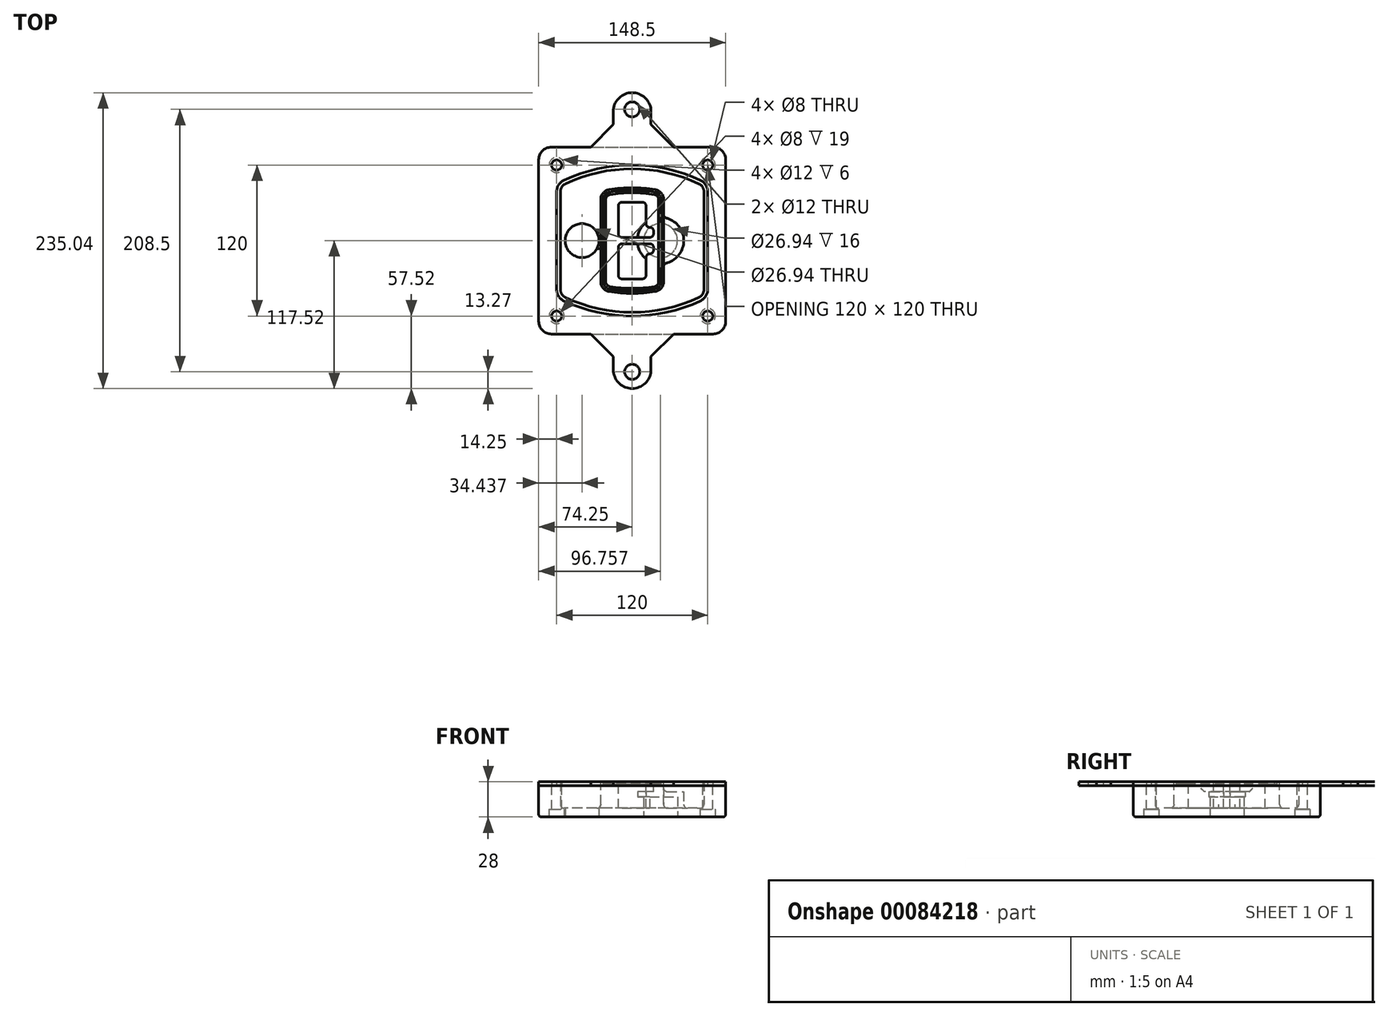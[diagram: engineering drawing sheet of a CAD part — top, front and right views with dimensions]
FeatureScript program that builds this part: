
annotation { "Feature Type Name" : "Feature", "Feature Type Description" : "" }
export const myFeature = defineFeature(function(context is Context, id is Id, definition is map)
    precondition{}
    {
        {
            var Q0;
            Q0=qCreatedBy(makeId("Top.planeOp"),FACE);
            var sketch = newSketch(context, id + "F0", { "sketchPlane" : qUnion([Q0])});
            skPoint(sketch, "E0.rect.middle", {"position": v(0, 0) * mm});
            skLineSegment(sketch, "E1.bottom", {"start": v(-64.25, -74.25) * mm, "end": v(64.25, -74.25) * mm});
            skLineSegment(sketch, "E1.top", {"start": v(-64.25, 74.25) * mm, "end": v(64.25, 74.25) * mm});
            skLineSegment(sketch, "E1.left", {"start": v(-74.25, -64.25) * mm, "end": v(-74.25, 64.25) * mm});
            skLineSegment(sketch, "E1.right", {"start": v(74.25, -64.25) * mm, "end": v(74.25, 64.25) * mm});
            skLineSegment(sketch, "E2", {"start": v(-74.25, 74.25) * mm, "end": v(74.25, -74.25) * mm, "construction": true});
            skLineSegment(sketch, "E3", {"start": v(74.25, 74.25) * mm, "end": v(-74.25, -74.25) * mm, "construction": true});
            skCircle(sketch, "E4", {"center": v(-60, 60) * mm, "radius": 4 * mm});
            skCircle(sketch, "E5", {"center": v(60, 60) * mm, "radius": 4 * mm});
            skCircle(sketch, "E6", {"center": v(60, -60) * mm, "radius": 4 * mm});
            skCircle(sketch, "E7", {"center": v(-60, -60) * mm, "radius": 4 * mm});
            skLineSegment(sketch, "E8", {"start": v(-60, 60) * mm, "end": v(60, 60) * mm, "construction": true});
            skLineSegment(sketch, "E9", {"start": v(60, 60) * mm, "end": v(60, -60) * mm, "construction": true});
            skLineSegment(sketch, "E10", {"start": v(60, -60) * mm, "end": v(-60, -60) * mm, "construction": true});
            skLineSegment(sketch, "E11", {"start": v(-60, -60) * mm, "end": v(-60, 60) * mm, "construction": true});
            skLineSegment(sketch, "E12", {"start": v(-60, 38.83) * mm, "end": v(-60, -38.83) * mm});
            skLineSegment(sketch, "E13", {"start": v(60, 38.83) * mm, "end": v(60, -38.83) * mm});
            skArc(sketch, "E14", {"start": v(54.26, 47.88) * mm, "mid": v(0, 60) * mm, "end": v(-54.26, 47.88) * mm});
            skArc(sketch, "E15", {"start": v(-54.26, -47.88) * mm, "mid": v(0, -60) * mm, "end": v(54.26, -47.88) * mm});
            skLineSegment(sketch, "E16", {"start": v(-60, 0) * mm, "end": v(60, 0) * mm, "construction": true});
            skPoint(sketch, "E17.visualSharp", {"position": v(-60, -45) * mm});
            skArc(sketch, "E17.filletArc", {"start": v(-60, -38.83) * mm, "mid": v(-58.44, -44.2) * mm, "end": v(-54.26, -47.88) * mm});
            skPoint(sketch, "E18.visualSharp", {"position": v(-60, 45) * mm});
            skArc(sketch, "E18.filletArc", {"start": v(-54.26, 47.88) * mm, "mid": v(-58.44, 44.2) * mm, "end": v(-60, 38.83) * mm});
            skPoint(sketch, "E19.visualSharp", {"position": v(60, 45) * mm});
            skArc(sketch, "E19.filletArc", {"start": v(60, 38.83) * mm, "mid": v(58.44, 44.2) * mm, "end": v(54.26, 47.88) * mm});
            skPoint(sketch, "E20.visualSharp", {"position": v(60, -45) * mm});
            skArc(sketch, "E20.filletArc", {"start": v(54.26, -47.88) * mm, "mid": v(58.44, -44.2) * mm, "end": v(60, -38.83) * mm});
            skPoint(sketch, "E21.visualSharp", {"position": v(-74.25, 74.25) * mm});
            skArc(sketch, "E21.filletArc", {"start": v(-64.25, 74.25) * mm, "mid": v(-71.32, 71.32) * mm, "end": v(-74.25, 64.25) * mm});
            skPoint(sketch, "E22.visualSharp", {"position": v(74.25, 74.25) * mm});
            skArc(sketch, "E22.filletArc", {"start": v(74.25, 64.25) * mm, "mid": v(71.32, 71.32) * mm, "end": v(64.25, 74.25) * mm});
            skPoint(sketch, "E23.visualSharp", {"position": v(74.25, -74.25) * mm});
            skArc(sketch, "E23.filletArc", {"start": v(64.25, -74.25) * mm, "mid": v(71.32, -71.32) * mm, "end": v(74.25, -64.25) * mm});
            skPoint(sketch, "E24.visualSharp", {"position": v(-74.25, -74.25) * mm});
            skArc(sketch, "E24.filletArc", {"start": v(-74.25, -64.25) * mm, "mid": v(-71.32, -71.32) * mm, "end": v(-64.25, -74.25) * mm});
            skArc(sketch, "E25.0", {"start": v(57, 38.83) * mm, "mid": v(55.9, 42.58) * mm, "end": v(52.98, 45.17) * mm});
            skLineSegment(sketch, "E25.1", {"start": v(57, 38.83) * mm, "end": v(57, -38.83) * mm});
            skArc(sketch, "E25.2", {"start": v(52.98, -45.17) * mm, "mid": v(55.9, -42.58) * mm, "end": v(57, -38.83) * mm});
            skArc(sketch, "E25.3", {"start": v(-52.98, -45.17) * mm, "mid": v(0, -57) * mm, "end": v(52.98, -45.17) * mm});
            skArc(sketch, "E25.4", {"start": v(-57, -38.83) * mm, "mid": v(-55.9, -42.58) * mm, "end": v(-52.98, -45.17) * mm});
            skArc(sketch, "E25.5", {"start": v(52.98, 45.17) * mm, "mid": v(0, 57) * mm, "end": v(-52.98, 45.17) * mm});
            skLineSegment(sketch, "E25.6", {"start": v(-57, 38.83) * mm, "end": v(-57, -38.83) * mm});
            skArc(sketch, "E25.7", {"start": v(-52.98, 45.17) * mm, "mid": v(-55.9, 42.58) * mm, "end": v(-57, 38.83) * mm});
            skArc(sketch, "E26.0", {"start": v(-55.96, 51.5) * mm, "mid": v(-61.82, 46.33) * mm, "end": v(-64, 38.83) * mm});
            skArc(sketch, "E26.1", {"start": v(55.96, 51.5) * mm, "mid": v(0, 64) * mm, "end": v(-55.96, 51.5) * mm});
            skArc(sketch, "E26.2", {"start": v(64, 38.83) * mm, "mid": v(61.82, 46.33) * mm, "end": v(55.96, 51.5) * mm});
            skLineSegment(sketch, "E26.3", {"start": v(64, 38.83) * mm, "end": v(64, -38.83) * mm});
            skArc(sketch, "E26.4", {"start": v(55.96, -51.5) * mm, "mid": v(61.82, -46.33) * mm, "end": v(64, -38.83) * mm});
            skLineSegment(sketch, "E26.5", {"start": v(-64, 38.83) * mm, "end": v(-64, -38.83) * mm});
            skArc(sketch, "E26.6", {"start": v(-55.96, -51.5) * mm, "mid": v(0, -64) * mm, "end": v(55.96, -51.5) * mm});
            skArc(sketch, "E26.7", {"start": v(-64, -38.83) * mm, "mid": v(-61.82, -46.33) * mm, "end": v(-55.96, -51.5) * mm});
            skSolve(sketch);
        }
        {
            var Q0;
            Q0=makeQuery(id+"F0.imprint","IMPRINT",FACE,{"disambiguationData":[TD([[makeQuery(id+"F0.imprint","IMPRINT",EDGE,{"derivedFrom":sQuery(id+"F0.wireOp",EDGE,"E1.bottom")}),1.0]])]});
            var Q1;
            Q1=makeQuery(id+"F0.imprint","IMPRINT",FACE,{"disambiguationData":[TD([[makeQuery(id+"F0.imprint","IMPRINT",EDGE,{"derivedFrom":sQuery(id+"F0.wireOp",EDGE,"E12")}),1.0]])]});
            var Q2;
            Q2=makeQuery(id+"F0.imprint","IMPRINT",FACE,{"disambiguationData":[TD([[makeQuery(id+"F0.imprint","IMPRINT",EDGE,{"derivedFrom":sQuery(id+"F0.wireOp",EDGE,"E25.0")}),1.0]])]});
            var Q3;
            Q3=makeQuery(id+"F0.imprint","IMPRINT",FACE,{"disambiguationData":[TD([[makeQuery(id+"F0.imprint","IMPRINT",EDGE,{"derivedFrom":sQuery(id+"F0.wireOp",EDGE,"E12")}),-1.0]])]});
            extrude(context, id + "F1", {"entities" : qUnion([Q0, Q1, Q2, Q3]), "oppositeDirection" : true, "depth" : 25 * mm});
        }
        {
            var Q0;
            Q0=makeQuery(id+"F0.imprint","IMPRINT",FACE,{"disambiguationData":[TD([[makeQuery(id+"F0.imprint","IMPRINT",EDGE,{"derivedFrom":sQuery(id+"F0.wireOp",EDGE,"E12")}),1.0]])]});
            extrude(context, id + "F2", {"entities" : qUnion([Q0]), "operationType" : NewBodyOperationType.ADD, "depth" : 3 * mm});
        }
        {
            var Q0;
            Q0=makeQuery(id+"F0.imprint","IMPRINT",FACE,{"disambiguationData":[TD([[makeQuery(id+"F0.imprint","IMPRINT",EDGE,{"derivedFrom":sQuery(id+"F0.wireOp",EDGE,"E25.0")}),1.0]])]});
            extrude(context, id + "F3", {"entities" : qUnion([Q0]), "operationType" : NewBodyOperationType.REMOVE, "oppositeDirection" : true, "depth" : 18 * mm});
        }
        {
            var Q0;
            Q0=makeQuery(id+"F2.opExtrude","CAP_FACE",FACE,{"disambiguationData":[OSD([sQuery(id+"F0.wireOp",EDGE,"E12"),sQuery(id+"F0.wireOp",EDGE,"E13"),sQuery(id+"F0.wireOp",EDGE,"E14"),sQuery(id+"F0.wireOp",EDGE,"E15"),sQuery(id+"F0.wireOp",EDGE,"E17.filletArc"),sQuery(id+"F0.wireOp",EDGE,"E18.filletArc"),sQuery(id+"F0.wireOp",EDGE,"E19.filletArc"),sQuery(id+"F0.wireOp",EDGE,"E20.filletArc"),sQuery(id+"F0.wireOp",EDGE,"E25.0"),sQuery(id+"F0.wireOp",EDGE,"E25.1"),sQuery(id+"F0.wireOp",EDGE,"E25.2"),sQuery(id+"F0.wireOp",EDGE,"E25.3"),sQuery(id+"F0.wireOp",EDGE,"E25.4"),sQuery(id+"F0.wireOp",EDGE,"E25.5"),sQuery(id+"F0.wireOp",EDGE,"E25.6"),sQuery(id+"F0.wireOp",EDGE,"E25.7")])],"isStart":false});
            var sketch = newSketch(context, id + "F4", { "sketchPlane" : qUnion([Q0])});
            skArc(sketch, "E27.0", {"start": v(-18.34, -40.45) * mm, "mid": v(0, -42) * mm, "end": v(18.34, -40.45) * mm});
            skArc(sketch, "E28.0", {"start": v(18.34, 40.45) * mm, "mid": v(0, 42) * mm, "end": v(-18.34, 40.45) * mm});
            skLineSegment(sketch, "E29", {"start": v(-25, 32.57) * mm, "end": v(-25, -32.57) * mm});
            skLineSegment(sketch, "E30", {"start": v(25, 32.57) * mm, "end": v(25, -32.57) * mm});
            skLineSegment(sketch, "E31", {"start": v(-25, 39.1) * mm, "end": v(25, 39.1) * mm, "construction": true});
            skLineSegment(sketch, "E32", {"start": v(-25, -39.1) * mm, "end": v(25, -39.1) * mm, "construction": true});
            skPoint(sketch, "E33.visualSharp", {"position": v(-25, 39.1) * mm});
            skArc(sketch, "E33.filletArc", {"start": v(-18.34, 40.45) * mm, "mid": v(-23.11, 37.73) * mm, "end": v(-25, 32.57) * mm});
            skPoint(sketch, "E34.visualSharp", {"position": v(25, 39.1) * mm});
            skArc(sketch, "E34.filletArc", {"start": v(25, 32.57) * mm, "mid": v(23.11, 37.73) * mm, "end": v(18.34, 40.45) * mm});
            skPoint(sketch, "E35.visualSharp", {"position": v(25, -39.1) * mm});
            skArc(sketch, "E35.filletArc", {"start": v(18.34, -40.45) * mm, "mid": v(23.11, -37.73) * mm, "end": v(25, -32.57) * mm});
            skPoint(sketch, "E36.visualSharp", {"position": v(-25, -39.1) * mm});
            skArc(sketch, "E36.filletArc", {"start": v(-25, -32.57) * mm, "mid": v(-23.11, -37.73) * mm, "end": v(-18.34, -40.45) * mm});
            skArc(sketch, "E37.0", {"start": v(52.98, 45.17) * mm, "mid": v(0, 57) * mm, "end": v(-52.98, 45.17) * mm});
            skArc(sketch, "E37.1", {"start": v(-52.98, 45.17) * mm, "mid": v(-55.9, 42.58) * mm, "end": v(-57, 38.83) * mm});
            skLineSegment(sketch, "E37.2", {"start": v(-57, 38.83) * mm, "end": v(-57, -38.83) * mm});
            skArc(sketch, "E37.3", {"start": v(-57, -38.83) * mm, "mid": v(-55.9, -42.58) * mm, "end": v(-52.98, -45.17) * mm});
            skArc(sketch, "E37.4", {"start": v(-52.98, -45.17) * mm, "mid": v(0, -57) * mm, "end": v(52.98, -45.17) * mm});
            skArc(sketch, "E37.5", {"start": v(52.98, -45.17) * mm, "mid": v(55.9, -42.58) * mm, "end": v(57, -38.83) * mm});
            skLineSegment(sketch, "E37.6", {"start": v(57, 38.83) * mm, "end": v(57, -38.83) * mm});
            skArc(sketch, "E37.7", {"start": v(57, 38.83) * mm, "mid": v(55.9, 42.58) * mm, "end": v(52.98, 45.17) * mm});
            skLineSegment(sketch, "E38.0", {"start": v(23, 32.57) * mm, "end": v(23, -32.57) * mm});
            skArc(sketch, "E38.1", {"start": v(18, -38.48) * mm, "mid": v(21.58, -36.44) * mm, "end": v(23, -32.57) * mm});
            skArc(sketch, "E38.2", {"start": v(-18, -38.48) * mm, "mid": v(0, -40) * mm, "end": v(18, -38.48) * mm});
            skArc(sketch, "E38.3", {"start": v(-23, -32.57) * mm, "mid": v(-21.58, -36.44) * mm, "end": v(-18, -38.48) * mm});
            skLineSegment(sketch, "E38.4", {"start": v(-23, 32.57) * mm, "end": v(-23, -32.57) * mm});
            skArc(sketch, "E38.5", {"start": v(23, 32.57) * mm, "mid": v(21.58, 36.44) * mm, "end": v(18, 38.48) * mm});
            skArc(sketch, "E38.6", {"start": v(-18, 38.48) * mm, "mid": v(-21.58, 36.44) * mm, "end": v(-23, 32.57) * mm});
            skArc(sketch, "E38.7", {"start": v(18, 38.48) * mm, "mid": v(0, 40) * mm, "end": v(-18, 38.48) * mm});
            skArc(sketch, "E39.0", {"start": v(21, 32.57) * mm, "mid": v(20.06, 35.15) * mm, "end": v(17.67, 36.5) * mm});
            skLineSegment(sketch, "E39.1", {"start": v(21, 32.57) * mm, "end": v(21, -32.57) * mm});
            skArc(sketch, "E39.2", {"start": v(17.67, -36.5) * mm, "mid": v(20.06, -35.15) * mm, "end": v(21, -32.57) * mm});
            skArc(sketch, "E39.3", {"start": v(-17.67, -36.5) * mm, "mid": v(0, -38) * mm, "end": v(17.67, -36.5) * mm});
            skArc(sketch, "E39.4", {"start": v(-21, -32.57) * mm, "mid": v(-20.06, -35.15) * mm, "end": v(-17.67, -36.5) * mm});
            skArc(sketch, "E39.5", {"start": v(17.67, 36.5) * mm, "mid": v(0, 38) * mm, "end": v(-17.67, 36.5) * mm});
            skLineSegment(sketch, "E39.6", {"start": v(-21, 32.57) * mm, "end": v(-21, -32.57) * mm});
            skArc(sketch, "E39.7", {"start": v(-17.67, 36.5) * mm, "mid": v(-20.06, 35.15) * mm, "end": v(-21, 32.57) * mm});
            skLineSegment(sketch, "E40", {"start": v(-25, 0) * mm, "end": v(25, 0) * mm, "construction": true});
            skLineSegment(sketch, "E41", {"start": v(-11, 5.5) * mm, "end": v(-11, 27.5) * mm});
            skLineSegment(sketch, "E42", {"start": v(-8, 30.5) * mm, "end": v(8, 30.5) * mm});
            skLineSegment(sketch, "E43", {"start": v(11, 27.5) * mm, "end": v(11, 13.5) * mm});
            skLineSegment(sketch, "E44", {"start": v(14, 10.5) * mm, "end": v(14, 10.5) * mm});
            skLineSegment(sketch, "E45", {"start": v(17, 7.5) * mm, "end": v(17, 5.5) * mm});
            skLineSegment(sketch, "E46", {"start": v(14, 2.5) * mm, "end": v(-8, 2.5) * mm});
            skPoint(sketch, "E47.visualSharp", {"position": v(-11, 30.5) * mm});
            skArc(sketch, "E47.filletArc", {"start": v(-8, 30.5) * mm, "mid": v(-10.12, 29.62) * mm, "end": v(-11, 27.5) * mm});
            skPoint(sketch, "E48.visualSharp", {"position": v(11, 30.5) * mm});
            skArc(sketch, "E48.filletArc", {"start": v(11, 27.5) * mm, "mid": v(10.12, 29.62) * mm, "end": v(8, 30.5) * mm});
            skPoint(sketch, "E49.visualSharp", {"position": v(11, 10.5) * mm});
            skArc(sketch, "E49.filletArc", {"start": v(11, 13.5) * mm, "mid": v(11.88, 11.38) * mm, "end": v(14, 10.5) * mm});
            skPoint(sketch, "E50.visualSharp", {"position": v(17, 10.5) * mm});
            skArc(sketch, "E50.filletArc", {"start": v(17, 7.5) * mm, "mid": v(16.12, 9.62) * mm, "end": v(14, 10.5) * mm});
            skPoint(sketch, "E51.visualSharp", {"position": v(17, 2.5) * mm});
            skArc(sketch, "E51.filletArc", {"start": v(14, 2.5) * mm, "mid": v(16.12, 3.38) * mm, "end": v(17, 5.5) * mm});
            skPoint(sketch, "E52.visualSharp", {"position": v(-11, 2.5) * mm});
            skArc(sketch, "E52.filletArc", {"start": v(-11, 5.5) * mm, "mid": v(-10.12, 3.38) * mm, "end": v(-8, 2.5) * mm});
            skLineSegment(sketch, "E53.0.MirrorCS", {"start": v(14, -2.5) * mm, "end": v(-8, -2.5) * mm});
            skArc(sketch, "E54.0.MirrorCS", {"start": v(-11, -5.5) * mm, "mid": v(-10.12, -3.38) * mm, "end": v(-8, -2.5) * mm});
            skLineSegment(sketch, "E55.0.MirrorCS", {"start": v(-11, -5.5) * mm, "end": v(-11, -27.5) * mm});
            skArc(sketch, "E56.0.MirrorCS", {"start": v(-8, -30.5) * mm, "mid": v(-10.12, -29.62) * mm, "end": v(-11, -27.5) * mm});
            skLineSegment(sketch, "E57.0.MirrorCS", {"start": v(-8, -30.5) * mm, "end": v(8, -30.5) * mm});
            skArc(sketch, "E58.0.MirrorCS", {"start": v(11, -27.5) * mm, "mid": v(10.12, -29.62) * mm, "end": v(8, -30.5) * mm});
            skLineSegment(sketch, "E59.0.MirrorCS", {"start": v(11, -27.5) * mm, "end": v(11, -13.5) * mm});
            skArc(sketch, "E60.0.MirrorCS", {"start": v(11, -13.5) * mm, "mid": v(11.88, -11.38) * mm, "end": v(14, -10.5) * mm});
            skArc(sketch, "E61.0.MirrorCS", {"start": v(17, -7.5) * mm, "mid": v(16.12, -9.62) * mm, "end": v(14, -10.5) * mm});
            skLineSegment(sketch, "E62.0.MirrorCS", {"start": v(17, -7.5) * mm, "end": v(17, -5.5) * mm});
            skArc(sketch, "E63.0.MirrorCS", {"start": v(14, -2.5) * mm, "mid": v(16.12, -3.38) * mm, "end": v(17, -5.5) * mm});
            skSolve(sketch);
        }
        {
            var Q0;
            Q0=makeQuery(id+"F4.imprint","IMPRINT",FACE,{"disambiguationData":[TD([[makeQuery(id+"F4.imprint","IMPRINT",EDGE,{"derivedFrom":sQuery(id+"F4.wireOp",EDGE,"E27.0")}),1.0]])]});
            var Q1;
            Q1=makeQuery(id+"F4.imprint","IMPRINT",FACE,{"disambiguationData":[TD([[makeQuery(id+"F4.imprint","IMPRINT",EDGE,{"derivedFrom":sQuery(id+"F4.wireOp",EDGE,"E38.0")}),-1.0]])]});
            var Q2;
            Q2=makeQuery(id+"F4.imprint","IMPRINT",FACE,{"disambiguationData":[TD([[makeQuery(id+"F4.imprint","IMPRINT",EDGE,{"derivedFrom":sQuery(id+"F4.wireOp",EDGE,"E39.0")}),1.0]])]});
            extrude(context, id + "F5", {"entities" : qUnion([Q0, Q1, Q2]), "operationType" : NewBodyOperationType.ADD, "endBound" : BoundingType.UP_TO_NEXT, "oppositeDirection" : true, "depth" : 25 * mm});
        }
        {
            var Q0;
            Q0=makeQuery(id+"F4.imprint","IMPRINT",FACE,{"disambiguationData":[TD([[makeQuery(id+"F4.imprint","IMPRINT",EDGE,{"derivedFrom":sQuery(id+"F4.wireOp",EDGE,"E38.0")}),-1.0]])]});
            extrude(context, id + "F6", {"entities" : qUnion([Q0]), "operationType" : NewBodyOperationType.REMOVE, "oppositeDirection" : true, "depth" : 2 * mm});
        }
        {
            var Q0;
            Q0=makeQuery(id+"F1.opExtrude","CAP_FACE",FACE,{"disambiguationData":[OSD([sQuery(id+"F0.wireOp",EDGE,"E1.bottom"),sQuery(id+"F0.wireOp",EDGE,"E1.top"),sQuery(id+"F0.wireOp",EDGE,"E1.left"),sQuery(id+"F0.wireOp",EDGE,"E1.right"),sQuery(id+"F0.wireOp",EDGE,"E4"),sQuery(id+"F0.wireOp",EDGE,"E5"),sQuery(id+"F0.wireOp",EDGE,"E6"),sQuery(id+"F0.wireOp",EDGE,"E7"),sQuery(id+"F0.wireOp",EDGE,"E21.filletArc"),sQuery(id+"F0.wireOp",EDGE,"E22.filletArc"),sQuery(id+"F0.wireOp",EDGE,"E23.filletArc"),sQuery(id+"F0.wireOp",EDGE,"E24.filletArc")])],"isStart":false});
            var sketch = newSketch(context, id + "F7", { "sketchPlane" : qUnion([Q0])});
            skCircle(sketch, "E64", {"center": v(22.5, 0) * mm, "radius": 13.47 * mm});
            skCircle(sketch, "E65", {"center": v(-39.81, 0) * mm, "radius": 13.47 * mm});
            skLineSegment(sketch, "E66", {"start": v(74.25, 0) * mm, "end": v(-74.25, 0) * mm});
            skCircle(sketch, "E67", {"center": v(22.5, 0) * mm, "radius": 18.47 * mm});
            skCircle(sketch, "E68", {"center": v(60, -60) * mm, "radius": 6 * mm});
            skCircle(sketch, "E69", {"center": v(-60, -60) * mm, "radius": 6 * mm});
            skCircle(sketch, "E70", {"center": v(-60, 60) * mm, "radius": 6 * mm});
            skCircle(sketch, "E71", {"center": v(60, 60) * mm, "radius": 6 * mm});
            skSolve(sketch);
        }
        {
            var Q0;
            {var subQ1=sQuery(id+"F7.wireOp",EDGE,"E66");var subQ4=sQuery(id+"F7.wireOp",EDGE,"E64");var subQ6=makeQuery(id+"F7.imprint","INTERSECT",VERTEX,{"disambiguationData":[OD(0.0)],"derivedFrom":[subQ4,subQ1]});Q0=makeQuery(id+"F7.imprint","IMPRINT",FACE,{"disambiguationData":[TD([[makeQuery(id+"F7.imprint","IMPRINT",EDGE,{"disambiguationData":[TD([[subQ6,-1.0]])],"derivedFrom":subQ4}),-1.0]])]});}
            var Q1;
            {var subQ0=sQuery(id+"F7.wireOp",EDGE,"E66");var subQ1=sQuery(id+"F7.wireOp",EDGE,"E64");var subQ3=makeQuery(id+"F7.imprint","INTERSECT",VERTEX,{"disambiguationData":[OD(0.0)],"derivedFrom":[subQ1,subQ0]});Q1=makeQuery(id+"F7.imprint","IMPRINT",FACE,{"disambiguationData":[TD([[makeQuery(id+"F7.imprint","IMPRINT",EDGE,{"disambiguationData":[TD([[subQ3,-1.0]])],"derivedFrom":subQ1}),1.0]])]});}
            var Q2;
            {var subQ0=sQuery(id+"F7.wireOp",EDGE,"E66");var subQ1=sQuery(id+"F7.wireOp",EDGE,"E64");var subQ3=makeQuery(id+"F7.imprint","INTERSECT",VERTEX,{"disambiguationData":[OD(0.0)],"derivedFrom":[subQ1,subQ0]});Q2=makeQuery(id+"F7.imprint","IMPRINT",FACE,{"disambiguationData":[TD([[makeQuery(id+"F7.imprint","IMPRINT",EDGE,{"disambiguationData":[TD([[subQ3,1.0]])],"derivedFrom":subQ1}),1.0]])]});}
            var Q3;
            {var subQ1=sQuery(id+"F7.wireOp",EDGE,"E66");var subQ4=sQuery(id+"F7.wireOp",EDGE,"E64");var subQ6=makeQuery(id+"F7.imprint","INTERSECT",VERTEX,{"disambiguationData":[OD(0.0)],"derivedFrom":[subQ4,subQ1]});Q3=makeQuery(id+"F7.imprint","IMPRINT",FACE,{"disambiguationData":[TD([[makeQuery(id+"F7.imprint","IMPRINT",EDGE,{"disambiguationData":[TD([[subQ6,1.0]])],"derivedFrom":subQ4}),-1.0]])]});}
            extrude(context, id + "F8", {"entities" : qUnion([Q0, Q1, Q2, Q3]), "operationType" : NewBodyOperationType.ADD, "oppositeDirection" : true, "depth" : 20 * mm});
        }
        {
            var Q0;
            {var subQ0=sQuery(id+"F7.wireOp",EDGE,"E66");var subQ1=sQuery(id+"F7.wireOp",EDGE,"E64");var subQ3=makeQuery(id+"F7.imprint","INTERSECT",VERTEX,{"disambiguationData":[OD(0.0)],"derivedFrom":[subQ1,subQ0]});Q0=makeQuery(id+"F7.imprint","IMPRINT",FACE,{"disambiguationData":[TD([[makeQuery(id+"F7.imprint","IMPRINT",EDGE,{"disambiguationData":[TD([[subQ3,-1.0]])],"derivedFrom":subQ1}),1.0]])]});}
            var Q1;
            {var subQ0=sQuery(id+"F7.wireOp",EDGE,"E66");var subQ1=sQuery(id+"F7.wireOp",EDGE,"E64");var subQ3=makeQuery(id+"F7.imprint","INTERSECT",VERTEX,{"disambiguationData":[OD(0.0)],"derivedFrom":[subQ1,subQ0]});Q1=makeQuery(id+"F7.imprint","IMPRINT",FACE,{"disambiguationData":[TD([[makeQuery(id+"F7.imprint","IMPRINT",EDGE,{"disambiguationData":[TD([[subQ3,1.0]])],"derivedFrom":subQ1}),1.0]])]});}
            extrude(context, id + "F9", {"entities" : qUnion([Q0, Q1]), "operationType" : NewBodyOperationType.REMOVE, "oppositeDirection" : true, "depth" : 16 * mm});
        }
        {
            var Q0;
            {var subQ0=sQuery(id+"F7.wireOp",EDGE,"E66");var subQ1=sQuery(id+"F7.wireOp",EDGE,"E65");var subQ3=makeQuery(id+"F7.imprint","INTERSECT",VERTEX,{"disambiguationData":[OD(0.0)],"derivedFrom":[subQ1,subQ0]});Q0=makeQuery(id+"F7.imprint","IMPRINT",FACE,{"disambiguationData":[TD([[makeQuery(id+"F7.imprint","IMPRINT",EDGE,{"disambiguationData":[TD([[subQ3,-1.0]])],"derivedFrom":subQ1}),1.0]])]});}
            var Q1;
            {var subQ0=sQuery(id+"F7.wireOp",EDGE,"E66");var subQ1=sQuery(id+"F7.wireOp",EDGE,"E65");var subQ3=makeQuery(id+"F7.imprint","INTERSECT",VERTEX,{"disambiguationData":[OD(0.0)],"derivedFrom":[subQ1,subQ0]});Q1=makeQuery(id+"F7.imprint","IMPRINT",FACE,{"disambiguationData":[TD([[makeQuery(id+"F7.imprint","IMPRINT",EDGE,{"disambiguationData":[TD([[subQ3,1.0]])],"derivedFrom":subQ1}),1.0]])]});}
            extrude(context, id + "F10", {"entities" : qUnion([Q0, Q1]), "operationType" : NewBodyOperationType.REMOVE, "oppositeDirection" : true, "depth" : 25 * mm});
        }
        {
            var Q0;
            Q0=makeQuery(id+"F7.imprint","IMPRINT",FACE,{"disambiguationData":[TD([[makeQuery(id+"F7.imprint","IMPRINT",EDGE,{"derivedFrom":sQuery(id+"F7.wireOp",EDGE,"E68")}),1.0]])]});
            var Q1;
            Q1=makeQuery(id+"F7.imprint","IMPRINT",FACE,{"disambiguationData":[TD([[makeQuery(id+"F7.imprint","IMPRINT",EDGE,{"derivedFrom":makeQuery(id+"F1.opExtrude","CAP_EDGE",EDGE,{"disambiguationData":[OSD([sQuery(id+"F0.wireOp",EDGE,"E5")])],"isStart":false})}),-1.0]])]});
            var Q2;
            Q2=makeQuery(id+"F7.imprint","IMPRINT",FACE,{"disambiguationData":[TD([[makeQuery(id+"F7.imprint","IMPRINT",EDGE,{"derivedFrom":sQuery(id+"F7.wireOp",EDGE,"E69")}),1.0]])]});
            var Q3;
            Q3=makeQuery(id+"F7.imprint","IMPRINT",FACE,{"disambiguationData":[TD([[makeQuery(id+"F7.imprint","IMPRINT",EDGE,{"derivedFrom":makeQuery(id+"F1.opExtrude","CAP_EDGE",EDGE,{"disambiguationData":[OSD([sQuery(id+"F0.wireOp",EDGE,"E4")])],"isStart":false})}),-1.0]])]});
            var Q4;
            Q4=makeQuery(id+"F7.imprint","IMPRINT",FACE,{"disambiguationData":[TD([[makeQuery(id+"F7.imprint","IMPRINT",EDGE,{"derivedFrom":sQuery(id+"F7.wireOp",EDGE,"E70")}),1.0]])]});
            var Q5;
            Q5=makeQuery(id+"F7.imprint","IMPRINT",FACE,{"disambiguationData":[TD([[makeQuery(id+"F7.imprint","IMPRINT",EDGE,{"derivedFrom":makeQuery(id+"F1.opExtrude","CAP_EDGE",EDGE,{"disambiguationData":[OSD([sQuery(id+"F0.wireOp",EDGE,"E7")])],"isStart":false})}),-1.0]])]});
            var Q6;
            Q6=makeQuery(id+"F7.imprint","IMPRINT",FACE,{"disambiguationData":[TD([[makeQuery(id+"F7.imprint","IMPRINT",EDGE,{"derivedFrom":sQuery(id+"F7.wireOp",EDGE,"E71")}),1.0]])]});
            var Q7;
            Q7=makeQuery(id+"F7.imprint","IMPRINT",FACE,{"disambiguationData":[TD([[makeQuery(id+"F7.imprint","IMPRINT",EDGE,{"derivedFrom":makeQuery(id+"F1.opExtrude","CAP_EDGE",EDGE,{"disambiguationData":[OSD([sQuery(id+"F0.wireOp",EDGE,"E6")])],"isStart":false})}),-1.0]])]});
            extrude(context, id + "F11", {"entities" : qUnion([Q0, Q1, Q2, Q3, Q4, Q5, Q6, Q7]), "operationType" : NewBodyOperationType.REMOVE, "oppositeDirection" : true, "depth" : 6 * mm});
        }
        {
            var Q0;
            Q0=makeQuery(id+"F9.boolean.opBoolean","COPY",FACE,{"derivedFrom":makeQuery(id+"F9.opExtrude","CAP_FACE",FACE,{"disambiguationData":[OSD([sQuery(id+"F7.wireOp",EDGE,"E64")])],"isStart":false})});
            var sketch = newSketch(context, id + "F12", { "sketchPlane" : qUnion([Q0])});
            skArc(sketch, "E72.0", {"start": v(11, 14.45) * mm, "mid": v(6.45, 9.13) * mm, "end": v(4.2, 2.5) * mm});
            skArc(sketch, "E72.1", {"start": v(4.2, -2.5) * mm, "mid": v(6.45, -9.13) * mm, "end": v(11, -14.45) * mm});
            skLineSegment(sketch, "E73", {"start": v(4.2, -2.5) * mm, "end": v(14, -2.5) * mm});
            skLineSegment(sketch, "E74.0", {"start": v(14, 2.5) * mm, "end": v(4.2, 2.5) * mm});
            skArc(sketch, "E74.1", {"start": v(14, 2.5) * mm, "mid": v(16.12, 3.38) * mm, "end": v(17, 5.5) * mm});
            skLineSegment(sketch, "E74.2", {"start": v(17, 7.5) * mm, "end": v(17, 5.5) * mm});
            skArc(sketch, "E74.3", {"start": v(17, 7.5) * mm, "mid": v(16.12, 9.62) * mm, "end": v(14, 10.5) * mm});
            skArc(sketch, "E74.4", {"start": v(11, 13.5) * mm, "mid": v(11.88, 11.38) * mm, "end": v(14, 10.5) * mm});
            skLineSegment(sketch, "E74.5", {"start": v(11, 14.45) * mm, "end": v(11, 13.5) * mm});
            skLineSegment(sketch, "E74.7", {"start": v(14, -2.5) * mm, "end": v(4.2, -2.5) * mm});
            skArc(sketch, "E74.8", {"start": v(14, -2.5) * mm, "mid": v(16.12, -3.38) * mm, "end": v(17, -5.5) * mm});
            skLineSegment(sketch, "E74.9", {"start": v(17, -7.5) * mm, "end": v(17, -5.5) * mm});
            skArc(sketch, "E74.10", {"start": v(17, -7.5) * mm, "mid": v(16.12, -9.62) * mm, "end": v(14, -10.5) * mm});
            skArc(sketch, "E74.11", {"start": v(11, -13.5) * mm, "mid": v(11.88, -11.38) * mm, "end": v(14, -10.5) * mm});
            skLineSegment(sketch, "E74.12", {"start": v(11, -14.45) * mm, "end": v(11, -13.5) * mm});
            skPoint(sketch, "E75.orphan", {"position": v(11, -27.5) * mm});
            skPoint(sketch, "E76.orphan", {"position": v(-8, -2.5) * mm});
            skPoint(sketch, "E77.orphan", {"position": v(-8, 2.5) * mm});
            skPoint(sketch, "E78.orphan", {"position": v(11, 27.5) * mm});
            skSolve(sketch);
        }
        {
            var Q0;
            {var subQ7=sQuery(id+"F12.wireOp",EDGE,"E72.0");var subQ14=sQuery(id+"F12.wireOp",EDGE,"E72.1");var subQ16=sQuery(id+"F12.wireOp",EDGE,"E74.1");var subQ18=sQuery(id+"F12.wireOp",EDGE,"E74.8");Q0=qUnion([makeQuery(id+"F12.imprint","IMPRINT",FACE,{"disambiguationData":[TD([[makeQuery(id+"F12.imprint","IMPRINT",EDGE,{"derivedFrom":subQ7}),1.0]])]}),makeQuery(id+"F12.imprint","IMPRINT",FACE,{"disambiguationData":[TD([[makeQuery(id+"F12.imprint","IMPRINT",EDGE,{"derivedFrom":subQ14}),1.0]])]}),makeQuery(id+"F12.imprint","IMPRINT",FACE,{"disambiguationData":[TD([[makeQuery(id+"F12.imprint","IMPRINT",EDGE,{"derivedFrom":subQ16}),1.0]])]}),makeQuery(id+"F12.imprint","IMPRINT",FACE,{"disambiguationData":[TD([[makeQuery(id+"F12.imprint","IMPRINT",EDGE,{"derivedFrom":subQ18}),-1.0]])]})]);}
            var Q1;
            Q1=makeQuery(id+"F5.boolean.opBoolean","SPLIT",FACE,{"disambiguationData":[TD([makeQuery(id+"F5.opExtrude","SWEPT_FACE",FACE,{"disambiguationData":[OSD([sQuery(id+"F4.wireOp",EDGE,"E41")])]})])],"derivedFrom":makeQuery(id+"F3.boolean.opBoolean","COPY",FACE,{"derivedFrom":makeQuery(id+"F3.opExtrude","CAP_FACE",FACE,{"disambiguationData":[OSD([sQuery(id+"F0.wireOp",EDGE,"E25.0"),sQuery(id+"F0.wireOp",EDGE,"E25.1"),sQuery(id+"F0.wireOp",EDGE,"E25.2"),sQuery(id+"F0.wireOp",EDGE,"E25.3"),sQuery(id+"F0.wireOp",EDGE,"E25.4"),sQuery(id+"F0.wireOp",EDGE,"E25.5"),sQuery(id+"F0.wireOp",EDGE,"E25.6"),sQuery(id+"F0.wireOp",EDGE,"E25.7")])],"isStart":false})})});
            extrude(context, id + "F13", {"entities" : qUnion([Q0]), "operationType" : NewBodyOperationType.REMOVE, "endBound" : BoundingType.UP_TO_SURFACE, "endBoundEntityFace" : qUnion([Q1]), "depth" : 25 * mm});
        }
        {
            var Q0;
            Q0=makeQuery(id+"F3.boolean.opBoolean","COPY",EDGE,{"derivedFrom":makeQuery(id+"F3.opExtrude","CAP_EDGE",EDGE,{"disambiguationData":[OSD([sQuery(id+"F0.wireOp",EDGE,"E25.6")])],"isStart":false})});
            var Q1;
            Q1=makeQuery(id+"F8.boolean.opBoolean","INTERSECT",EDGE,{"derivedFrom":[makeQuery(id+"F5.opExtrude","SWEPT_FACE",FACE,{"disambiguationData":[OSD([sQuery(id+"F4.wireOp",EDGE,"E30")])]}),makeQuery(id+"F8.opExtrude","CAP_FACE",FACE,{"disambiguationData":[OSD([sQuery(id+"F7.wireOp",EDGE,"E67")])],"isStart":false})]});
            var Q2;
            Q2=makeQuery(id+"F8.boolean.opBoolean","INTERSECT",EDGE,{"disambiguationData":[OD(1.0)],"derivedFrom":[makeQuery(id+"F5.opExtrude","SWEPT_FACE",FACE,{"disambiguationData":[OSD([sQuery(id+"F4.wireOp",EDGE,"E30")])]}),makeQuery(id+"F8.opExtrude","SWEPT_FACE",FACE,{"disambiguationData":[OSD([sQuery(id+"F7.wireOp",EDGE,"E67")])]})]});
            var Q3;
            {var subQ0=sQuery(id+"F4.wireOp",EDGE,"E30");Q3=makeQuery(id+"F8.boolean.opBoolean","SPLIT",EDGE,{"disambiguationData":[TD([makeQuery(id+"F5.opExtrude","SWEPT_FACE",FACE,{"disambiguationData":[OSD([sQuery(id+"F4.wireOp",EDGE,"E35.filletArc")])]})])],"derivedFrom":makeQuery(id+"F5.opExtrude","CAP_EDGE",EDGE,{"disambiguationData":[OSD([subQ0])],"isStart":false})});}
            var Q4;
            {var subQ0=sQuery(id+"F0.wireOp",EDGE,"E25.7");var subQ1=sQuery(id+"F0.wireOp",EDGE,"E25.1");var subQ2=sQuery(id+"F0.wireOp",EDGE,"E25.6");var subQ3=sQuery(id+"F0.wireOp",EDGE,"E25.5");var subQ4=sQuery(id+"F0.wireOp",EDGE,"E25.4");var subQ5=sQuery(id+"F0.wireOp",EDGE,"E25.0");var subQ6=sQuery(id+"F0.wireOp",EDGE,"E25.2");var subQ7=sQuery(id+"F0.wireOp",EDGE,"E25.3");Q4=makeQuery(id+"F8.boolean.opBoolean","INTERSECT",EDGE,{"derivedFrom":[makeQuery(id+"F5.boolean.opBoolean","SPLIT",FACE,{"disambiguationData":[TD([makeQuery(id+"F2.opExtrude","SWEPT_FACE",FACE,{"disambiguationData":[OSD([subQ5])]})])],"derivedFrom":makeQuery(id+"F3.boolean.opBoolean","COPY",FACE,{"derivedFrom":makeQuery(id+"F3.opExtrude","CAP_FACE",FACE,{"disambiguationData":[OSD([subQ5,subQ1,subQ6,subQ7,subQ4,subQ3,subQ2,subQ0])],"isStart":false})})}),makeQuery(id+"F8.opExtrude","SWEPT_FACE",FACE,{"disambiguationData":[OSD([sQuery(id+"F7.wireOp",EDGE,"E67")])]})]});}
            var Q5;
            Q5=makeQuery(id+"F8.boolean.opBoolean","INTERSECT",EDGE,{"disambiguationData":[OD(0.0)],"derivedFrom":[makeQuery(id+"F5.opExtrude","SWEPT_FACE",FACE,{"disambiguationData":[OSD([sQuery(id+"F4.wireOp",EDGE,"E30")])]}),makeQuery(id+"F8.opExtrude","SWEPT_FACE",FACE,{"disambiguationData":[OSD([sQuery(id+"F7.wireOp",EDGE,"E67")])]})]});
            fillet(context, id + "F14", {"entities" : qUnion([Q0, Q1, Q2, Q3, Q4, Q5]), "radius" : 3 * mm, "tangentPropagation" : true, "allowEdgeOverflow" : false});
        }
        {
            var Q0;
            Q0=makeQuery(id+"F1.opExtrude","CAP_EDGE",EDGE,{"disambiguationData":[OSD([sQuery(id+"F0.wireOp",EDGE,"E1.bottom")])],"isStart":false});
            fillet(context, id + "F15", {"entities" : qUnion([Q0]), "radius" : 2 * mm, "tangentPropagation" : true, "allowEdgeOverflow" : false});
        }
        {
            var Q0;
            {var subQ0=sQuery(id+"F0.wireOp",EDGE,"E22.filletArc");var subQ1=sQuery(id+"F0.wireOp",EDGE,"E7");var subQ2=sQuery(id+"F0.wireOp",EDGE,"E6");var subQ3=sQuery(id+"F0.wireOp",EDGE,"E5");var subQ4=sQuery(id+"F0.wireOp",EDGE,"E4");var subQ5=sQuery(id+"F0.wireOp",EDGE,"E1.bottom");var subQ6=sQuery(id+"F0.wireOp",EDGE,"E21.filletArc");var subQ7=sQuery(id+"F0.wireOp",EDGE,"E1.top");var subQ8=sQuery(id+"F0.wireOp",EDGE,"E1.left");var subQ9=sQuery(id+"F0.wireOp",EDGE,"E1.right");var subQ10=sQuery(id+"F0.wireOp",EDGE,"E23.filletArc");var subQ11=sQuery(id+"F0.wireOp",EDGE,"E24.filletArc");Q0=makeQuery(id+"F2.boolean.opBoolean","SPLIT",FACE,{"disambiguationData":[TD([makeQuery(id+"F1.opExtrude","SWEPT_FACE",FACE,{"disambiguationData":[OSD([subQ5])]})])],"derivedFrom":makeQuery(id+"F1.opExtrude","CAP_FACE",FACE,{"disambiguationData":[OSD([subQ5,subQ7,subQ8,subQ9,subQ4,subQ3,subQ2,subQ1,subQ6,subQ0,subQ10,subQ11])],"isStart":true})});}
            var sketch = newSketch(context, id + "F16", { "sketchPlane" : qUnion([Q0])});
            skLineSegment(sketch, "E79", {"start": v(0, 74.25) * mm, "end": v(0, 104.25) * mm, "construction": true});
            skCircle(sketch, "E80", {"center": v(0, 104.25) * mm, "radius": 6 * mm});
            skArc(sketch, "E81", {"start": v(14.92, 104.02) * mm, "mid": v(-0.19, 117.52) * mm, "end": v(-14.96, 103.64) * mm});
            skLineSegment(sketch, "E82", {"start": v(-32.96, 74.25) * mm, "end": v(-14.96, 92.25) * mm});
            skLineSegment(sketch, "E83", {"start": v(-14.96, 103.64) * mm, "end": v(-14.96, 92.25) * mm});
            skLineSegment(sketch, "E84", {"start": v(14.92, 92.25) * mm, "end": v(32.92, 74.25) * mm});
            skLineSegment(sketch, "E85", {"start": v(14.92, 104.02) * mm, "end": v(14.92, 92.25) * mm});
            skArc(sketch, "E86.MirrorCS", {"start": v(-14.92, 104.02) * mm, "mid": v(0.19, 117.52) * mm, "end": v(14.96, 103.64) * mm});
            skLineSegment(sketch, "E87.MirrorCS", {"start": v(-14.92, 92.25) * mm, "end": v(-32.92, 74.25) * mm});
            skLineSegment(sketch, "E88.MirrorCS", {"start": v(-14.92, 104.02) * mm, "end": v(-14.92, 92.25) * mm});
            skLineSegment(sketch, "E89.MirrorCS", {"start": v(14.96, 103.64) * mm, "end": v(14.96, 92.25) * mm});
            skLineSegment(sketch, "E90.MirrorCS", {"start": v(32.96, 74.25) * mm, "end": v(14.96, 92.25) * mm});
            skLineSegment(sketch, "E91", {"start": v(-74.25, 0) * mm, "end": v(74.25, 0) * mm, "construction": true});
            skLineSegment(sketch, "E92.MirrorCS", {"start": v(-14.92, -92.25) * mm, "end": v(-32.92, -74.25) * mm});
            skLineSegment(sketch, "E93.MirrorCS", {"start": v(-14.92, -104.02) * mm, "end": v(-14.92, -92.25) * mm});
            skArc(sketch, "E94.MirrorCS", {"start": v(-14.92, -104.02) * mm, "mid": v(0.19, -117.52) * mm, "end": v(14.96, -103.64) * mm});
            skCircle(sketch, "E95.MirrorC", {"center": v(0, -104.25) * mm, "radius": 6 * mm});
            skLineSegment(sketch, "E96.MirrorCS", {"start": v(0, -74.25) * mm, "end": v(0, -104.25) * mm, "construction": true});
            skLineSegment(sketch, "E97.MirrorCS", {"start": v(14.96, -103.64) * mm, "end": v(14.96, -92.25) * mm});
            skLineSegment(sketch, "E98.MirrorCS", {"start": v(32.96, -74.25) * mm, "end": v(14.96, -92.25) * mm});
            skSolve(sketch);
        }
        {
            var Q0;
            {var subQ0=sQuery(id+"F16.wireOp",EDGE,"E92.MirrorCS");Q0=makeQuery(id+"F16.imprint","IMPRINT",FACE,{"disambiguationData":[TD([[makeQuery(id+"F16.imprint","IMPRINT",EDGE,{"derivedFrom":subQ0}),-1.0]])]});}
            var Q1;
            Q1=makeQuery(id+"F16.imprint","IMPRINT",FACE,{"disambiguationData":[TD([[makeQuery(id+"F16.imprint","IMPRINT",EDGE,{"derivedFrom":makeQuery(id+"F1.opExtrude","CAP_EDGE",EDGE,{"disambiguationData":[OSD([sQuery(id+"F0.wireOp",EDGE,"E1.left")])],"isStart":true})}),-1.0]])]});
            var Q2;
            {var subQ5=sQuery(id+"F16.wireOp",EDGE,"E84");Q2=makeQuery(id+"F16.imprint","IMPRINT",FACE,{"disambiguationData":[TD([[makeQuery(id+"F16.imprint","IMPRINT",EDGE,{"derivedFrom":subQ5}),-1.0]])]});}
            var Q3;
            Q3=makeQuery(id+"F2.opExtrude","CAP_FACE",FACE,{"disambiguationData":[OSD([sQuery(id+"F0.wireOp",EDGE,"E12"),sQuery(id+"F0.wireOp",EDGE,"E13"),sQuery(id+"F0.wireOp",EDGE,"E14"),sQuery(id+"F0.wireOp",EDGE,"E15"),sQuery(id+"F0.wireOp",EDGE,"E17.filletArc"),sQuery(id+"F0.wireOp",EDGE,"E18.filletArc"),sQuery(id+"F0.wireOp",EDGE,"E19.filletArc"),sQuery(id+"F0.wireOp",EDGE,"E20.filletArc"),sQuery(id+"F0.wireOp",EDGE,"E25.0"),sQuery(id+"F0.wireOp",EDGE,"E25.1"),sQuery(id+"F0.wireOp",EDGE,"E25.2"),sQuery(id+"F0.wireOp",EDGE,"E25.3"),sQuery(id+"F0.wireOp",EDGE,"E25.4"),sQuery(id+"F0.wireOp",EDGE,"E25.5"),sQuery(id+"F0.wireOp",EDGE,"E25.6"),sQuery(id+"F0.wireOp",EDGE,"E25.7")])],"isStart":false});
            var Q4;
            Q4=makeQuery(id+"F1.opExtrude","SWEPT_BODY",BODY,{"disambiguationData":[OSD([sQuery(id+"F0.wireOp",EDGE,"E1.bottom"),sQuery(id+"F0.wireOp",EDGE,"E1.top"),sQuery(id+"F0.wireOp",EDGE,"E1.left"),sQuery(id+"F0.wireOp",EDGE,"E1.right"),sQuery(id+"F0.wireOp",EDGE,"E4"),sQuery(id+"F0.wireOp",EDGE,"E5"),sQuery(id+"F0.wireOp",EDGE,"E6"),sQuery(id+"F0.wireOp",EDGE,"E7"),sQuery(id+"F0.wireOp",EDGE,"E21.filletArc"),sQuery(id+"F0.wireOp",EDGE,"E22.filletArc"),sQuery(id+"F0.wireOp",EDGE,"E23.filletArc"),sQuery(id+"F0.wireOp",EDGE,"E24.filletArc")])]});
            extrude(context, id + "F17", {"entities" : qUnion([Q0, Q1, Q2]), "endBound" : BoundingType.UP_TO_SURFACE, "endBoundEntityFace" : qUnion([Q3]), "endBoundEntityBody" : qUnion([Q4]), "depth" : 25 * mm});
        }
    });
